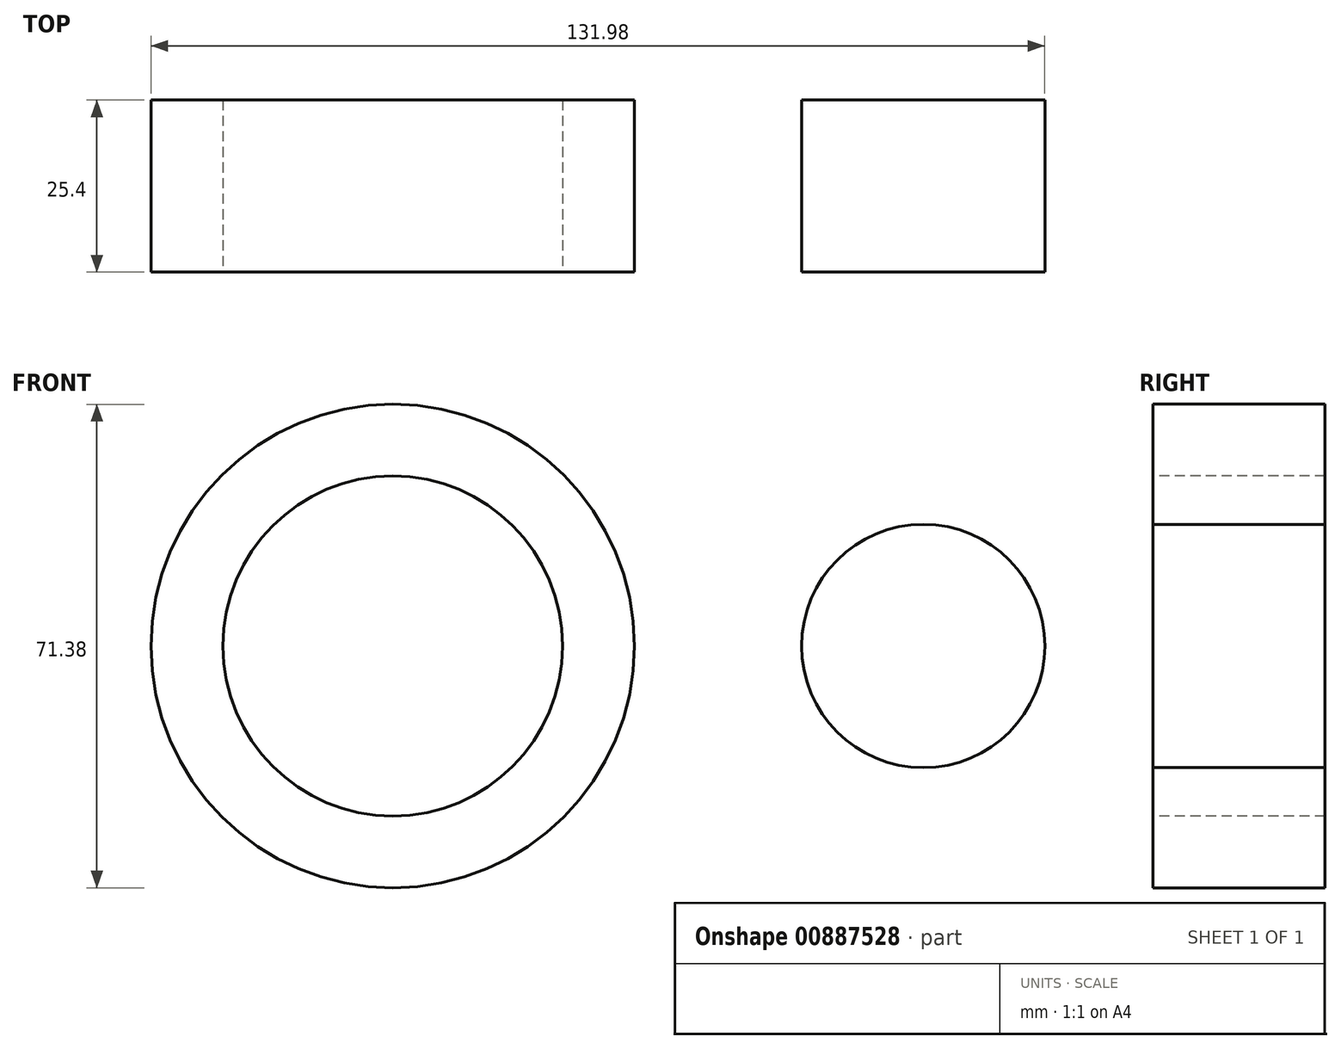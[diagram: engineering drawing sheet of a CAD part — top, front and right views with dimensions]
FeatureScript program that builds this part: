
annotation { "Feature Type Name" : "Feature", "Feature Type Description" : "" }
export const myFeature = defineFeature(function(context is Context, id is Id, definition is map)
    precondition{}
    {
        {
            var Q0;
            Q0=qCreatedBy(makeId("Front.planeOp"),FACE);
            var sketch = newSketch(context, id + "F0", { "sketchPlane" : qUnion([Q0])});
            skCircle(sketch, "E0", {"center": v(0, 0) * mm, "radius": 35.7 * mm});
            skSolve(sketch);
        }
        {
            var Q0;
            Q0=sQuery(id+"F0.wireOp",EDGE,"E0");
            extrude(context, id + "F1", {"bodyType" : ToolBodyType.SURFACE, "surfaceEntities" : qUnion([Q0]), "depth" : 25.4 * mm, "offsetDistance" : 25.4 * mm});
        }
        {
            var Q0;
            Q0=qCreatedBy(makeId("Front.planeOp"),FACE);
            var sketch = newSketch(context, id + "F2", { "sketchPlane" : qUnion([Q0])});
            skCircle(sketch, "E1", {"center": v(0, 0) * mm, "radius": 25.09 * mm});
            skCircle(sketch, "E2", {"center": v(78.34, 0) * mm, "radius": 17.96 * mm});
            skLineSegment(sketch, "E3", {"start": v(8.73, 34.44) * mm, "end": v(75.34, 17.7) * mm});
            skLineSegment(sketch, "E4", {"start": v(5.38, -35.4) * mm, "end": v(82.4, -17.5) * mm});
            skSolve(sketch);
        }
        {
            var Q0;
            Q0=sQuery(id+"F2.wireOp",EDGE,"E1");
            var Q1;
            Q1=sQuery(id+"F2.wireOp",EDGE,"E2");
            extrude(context, id + "F3", {"bodyType" : ToolBodyType.SURFACE, "surfaceEntities" : qUnion([Q0, Q1]), "depth" : 25.4 * mm, "offsetDistance" : 25.4 * mm});
        }
    });
